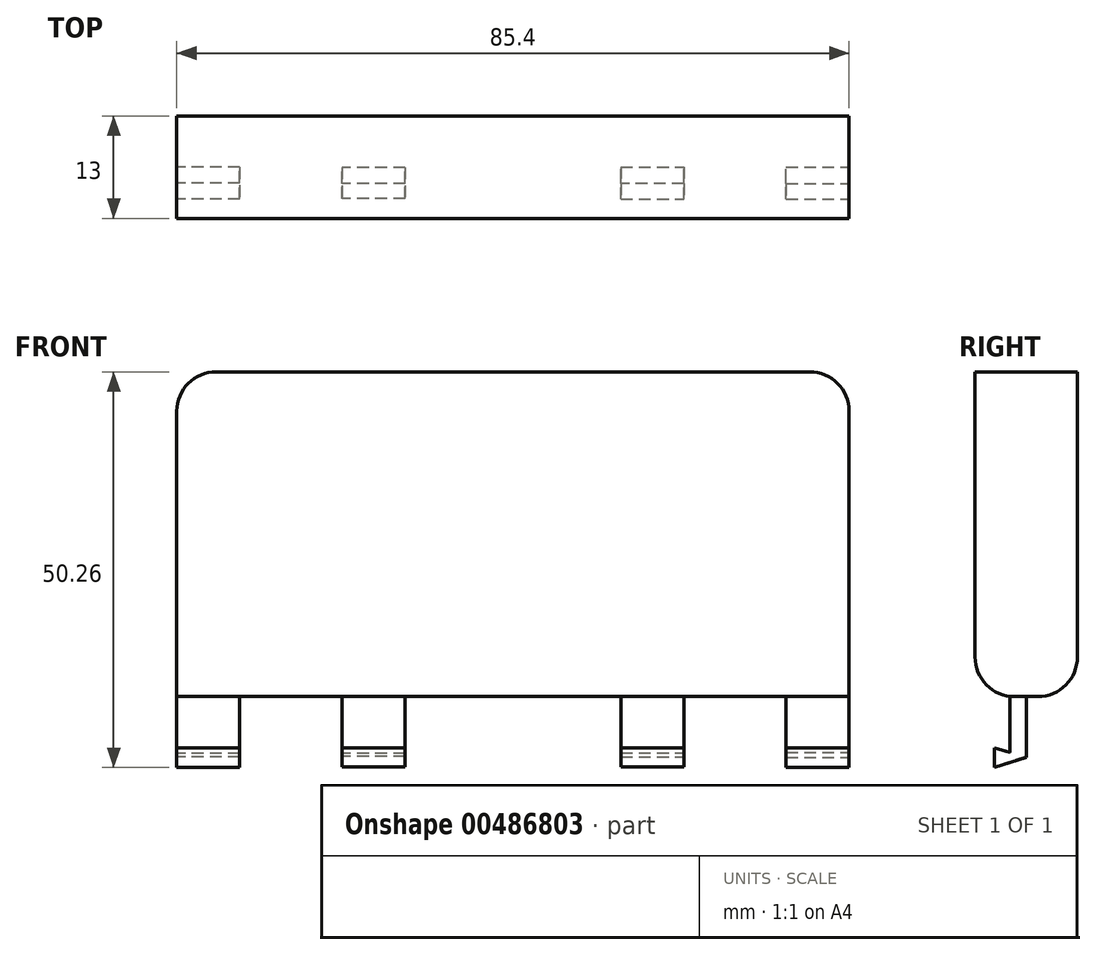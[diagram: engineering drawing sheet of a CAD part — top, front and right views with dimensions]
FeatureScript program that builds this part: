
annotation { "Feature Type Name" : "Feature", "Feature Type Description" : "" }
export const myFeature = defineFeature(function(context is Context, id is Id, definition is map)
    precondition{}
    {
        {
            var Q0;
            Q0=qCreatedBy(makeId("Front.planeOp"),FACE);
            var sketch = newSketch(context, id + "F0", { "sketchPlane" : qUnion([Q0])});
            skLineSegment(sketch, "E0.bottom", {"start": v(0, 0) * mm, "end": v(85.4, 0) * mm});
            skLineSegment(sketch, "E0.top", {"start": v(0, 41.24) * mm, "end": v(85.4, 41.24) * mm});
            skLineSegment(sketch, "E0.left", {"start": v(0, 0) * mm, "end": v(0, 41.24) * mm});
            skLineSegment(sketch, "E0.right", {"start": v(85.4, 0) * mm, "end": v(85.4, 41.24) * mm});
            skSolve(sketch);
        }
        {
            var Q0;
            Q0=makeQuery(id+"F0.imprint","IMPRINT",FACE,{"disambiguationData":[TD([[makeQuery(id+"F0.imprint","IMPRINT",EDGE,{"derivedFrom":sQuery(id+"F0.wireOp",EDGE,"E0.bottom")}),1.0]])]});
            extrude(context, id + "F1", {"entities" : qUnion([Q0]), "depth" : 13 * mm});
        }
        {
            var Q0;
            Q0=makeQuery(id+"F1.opExtrude","SWEPT_FACE",FACE,{"disambiguationData":[OSD([sQuery(id+"F0.wireOp",EDGE,"E0.left")])]});
            var sketch = newSketch(context, id + "F2", { "sketchPlane" : qUnion([Q0])});
            skLineSegment(sketch, "E1", {"start": v(6.5, 0) * mm, "end": v(6.5, -7.7) * mm});
            skLineSegment(sketch, "E2", {"start": v(8.5, -6.51) * mm, "end": v(8.5, 0) * mm});
            skLineSegment(sketch, "E3", {"start": v(6.5, -7.7) * mm, "end": v(10.56, -9) * mm});
            skLineSegment(sketch, "E4", {"start": v(10.56, -9) * mm, "end": v(10.56, -6.51) * mm});
            skLineSegment(sketch, "E5", {"start": v(10.56, -6.51) * mm, "end": v(8.5, -7.25) * mm});
            skLineSegment(sketch, "E6", {"start": v(8.5, -7.25) * mm, "end": v(8.5, -6.51) * mm});
            skSolve(sketch);
        }
        {
            var Q0;
            {var subQ1=sQuery(id+"F2.wireOp",EDGE,"E1");Q0=makeQuery(id+"F2.imprint","IMPRINT",FACE,{"disambiguationData":[TD([[makeQuery(id+"F2.imprint","IMPRINT",EDGE,{"derivedFrom":subQ1}),1.0]])]});}
            extrude(context, id + "F3", {"entities" : qUnion([Q0]), "oppositeDirection" : true, "depth" : 8 * mm});
        }
        {
            var Q0;
            Q0=makeQuery(id+"F1.opExtrude","SWEPT_FACE",FACE,{"disambiguationData":[OSD([sQuery(id+"F0.wireOp",EDGE,"E0.left")])]});
            cPlane(context, id + "F4", {"entities" : qUnion([Q0]), "cplaneType" : CPlaneType.OFFSET, "offset" : 21 * mm, "oppositeDirection" : true, "width" : 150 * mm, "height" : 150 * mm});
        }
        {
            var Q0;
            Q0=qCreatedBy(id+"F4.planeOp",FACE);
            var sketch = newSketch(context, id + "F5", { "sketchPlane" : qUnion([Q0])});
            skLineSegment(sketch, "E7", {"start": v(6.52, 0) * mm, "end": v(6.52, -7.62) * mm});
            skLineSegment(sketch, "E8", {"start": v(6.52, -7.62) * mm, "end": v(10.51, -8.92) * mm});
            skLineSegment(sketch, "E9", {"start": v(10.51, -8.92) * mm, "end": v(10.51, -6.55) * mm});
            skLineSegment(sketch, "E10", {"start": v(10.51, -6.55) * mm, "end": v(8.58, -7.23) * mm});
            skLineSegment(sketch, "E11", {"start": v(8.58, -7.23) * mm, "end": v(8.58, 0) * mm});
            skLineSegment(sketch, "E12", {"start": v(8.58, 0) * mm, "end": v(6.52, 0) * mm});
            skSolve(sketch);
        }
        {
            var Q0;
            Q0 = qSketchRegion(id + "F5", true);
            var Q1;
            Q1=makeQuery(id+"F3.opExtrude","CAP_FACE",FACE,{"disambiguationData":[OSD([sQuery(id+"F0.wireOp",EDGE,"E0.bottom"),sQuery(id+"F0.wireOp",EDGE,"E0.left"),sQuery(id+"F2.wireOp",EDGE,"E1"),sQuery(id+"F2.wireOp",EDGE,"E2"),sQuery(id+"F2.wireOp",EDGE,"E3"),sQuery(id+"F2.wireOp",EDGE,"E4"),sQuery(id+"F2.wireOp",EDGE,"E5"),sQuery(id+"F2.wireOp",EDGE,"E6")])],"isStart":true});
            extrude(context, id + "F6", {"entities" : qUnion([Q0, Q1]), "oppositeDirection" : true, "depth" : 8 * mm});
        }
        {
            var Q0;
            Q0=makeQuery(id+"F1.opExtrude","SWEPT_FACE",FACE,{"disambiguationData":[OSD([sQuery(id+"F0.wireOp",EDGE,"E0.right")])]});
            cPlane(context, id + "F7", {"entities" : qUnion([Q0]), "cplaneType" : CPlaneType.OFFSET, "offset" : 21 * mm, "oppositeDirection" : true, "width" : 150 * mm, "height" : 150 * mm});
        }
        {
            var Q0;
            Q0=qCreatedBy(id+"F7.planeOp",FACE);
            var sketch = newSketch(context, id + "F8", { "sketchPlane" : qUnion([Q0])});
            skLineSegment(sketch, "E13", {"start": v(-8.57, 0) * mm, "end": v(-8.57, -7.14) * mm});
            skLineSegment(sketch, "E14", {"start": v(-8.57, -7.14) * mm, "end": v(-10.56, -6.54) * mm});
            skLineSegment(sketch, "E15", {"start": v(-10.56, -6.54) * mm, "end": v(-10.56, -8.93) * mm});
            skLineSegment(sketch, "E16", {"start": v(-10.56, -8.93) * mm, "end": v(-6.48, -7.67) * mm});
            skLineSegment(sketch, "E17", {"start": v(-6.48, -7.67) * mm, "end": v(-6.48, 0) * mm});
            skLineSegment(sketch, "E18", {"start": v(-6.48, 0) * mm, "end": v(-8.57, 0) * mm});
            skSolve(sketch);
        }
        {
            var Q0;
            Q0=makeQuery(id+"F8.imprint","IMPRINT",FACE,{"disambiguationData":[TD([[makeQuery(id+"F8.imprint","IMPRINT",EDGE,{"derivedFrom":sQuery(id+"F8.wireOp",EDGE,"E13")}),1.0]])]});
            extrude(context, id + "F9", {"entities" : qUnion([Q0]), "operationType" : NewBodyOperationType.ADD, "oppositeDirection" : true, "depth" : 8 * mm});
        }
        {
            var Q0;
            Q0=makeQuery(id+"F1.opExtrude","SWEPT_FACE",FACE,{"disambiguationData":[OSD([sQuery(id+"F0.wireOp",EDGE,"E0.right")])]});
            var sketch = newSketch(context, id + "F10", { "sketchPlane" : qUnion([Q0])});
            skLineSegment(sketch, "E19", {"start": v(-8.6, 0) * mm, "end": v(-8.6, -7.12) * mm});
            skLineSegment(sketch, "E20", {"start": v(-8.6, -7.12) * mm, "end": v(-10.53, -6.5) * mm});
            skLineSegment(sketch, "E21", {"start": v(-10.53, -6.5) * mm, "end": v(-10.53, -9.02) * mm});
            skLineSegment(sketch, "E22", {"start": v(-10.53, -9.02) * mm, "end": v(-6.46, -7.7) * mm});
            skLineSegment(sketch, "E23", {"start": v(-6.46, -7.7) * mm, "end": v(-6.46, 0) * mm});
            skLineSegment(sketch, "E24", {"start": v(-6.46, 0) * mm, "end": v(-8.6, 0) * mm});
            skSolve(sketch);
        }
        {
            var Q0;
            Q0=makeQuery(id+"F10.imprint","IMPRINT",FACE,{"disambiguationData":[TD([[makeQuery(id+"F10.imprint","IMPRINT",EDGE,{"derivedFrom":sQuery(id+"F10.wireOp",EDGE,"E19")}),1.0]])]});
            extrude(context, id + "F11", {"entities" : qUnion([Q0]), "oppositeDirection" : true, "depth" : 8 * mm});
        }
        {
            var Q0;
            Q0=makeQuery(id+"F1.opExtrude","SWEPT_EDGE",EDGE,{"disambiguationData":[OSD([sQuery(id+"F0.wireOp",EDGE,"E0.top"),sQuery(id+"F0.wireOp",EDGE,"E0.left")])]});
            var Q1;
            Q1=makeQuery(id+"F1.opExtrude","SWEPT_EDGE",EDGE,{"disambiguationData":[OSD([sQuery(id+"F0.wireOp",EDGE,"E0.top"),sQuery(id+"F0.wireOp",EDGE,"E0.right")])]});
            fillet(context, id + "F12", {"entities" : qUnion([Q0, Q1]), "radius" : 5 * mm, "tangentPropagation" : true, "allowEdgeOverflow" : false});
        }
        {
            var Q0;
            Q0=makeQuery(id+"F1.opExtrude","CAP_EDGE",EDGE,{"disambiguationData":[OSD([sQuery(id+"F0.wireOp",EDGE,"E0.bottom")])],"isStart":false});
            var Q1;
            Q1=makeQuery(id+"F1.opExtrude","CAP_EDGE",EDGE,{"disambiguationData":[OSD([sQuery(id+"F0.wireOp",EDGE,"E0.bottom")])],"isStart":true});
            fillet(context, id + "F13", {"entities" : qUnion([Q0, Q1]), "radius" : 5 * mm, "tangentPropagation" : true, "allowEdgeOverflow" : false});
        }
    });
